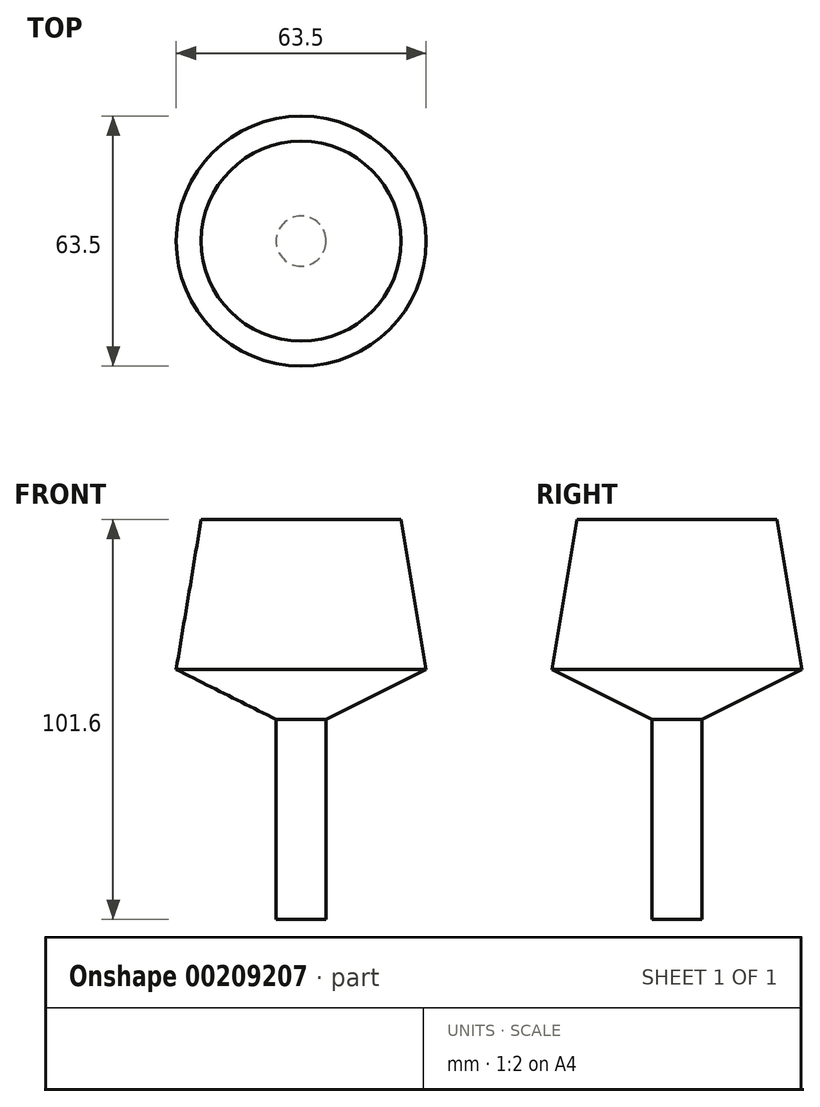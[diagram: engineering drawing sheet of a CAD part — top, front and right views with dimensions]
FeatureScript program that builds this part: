
annotation { "Feature Type Name" : "Feature", "Feature Type Description" : "" }
export const myFeature = defineFeature(function(context is Context, id is Id, definition is map)
    precondition{}
    {
        {
            var Q0;
            Q0=qCreatedBy(makeId("Front.planeOp"),FACE);
            var sketch = newSketch(context, id + "F0", { "sketchPlane" : qUnion([Q0])});
            skLineSegment(sketch, "E0", {"start": v(0, 0) * mm, "end": v(0, 101.6) * mm});
            skLineSegment(sketch, "E1", {"start": v(0, 101.6) * mm, "end": v(25.4, 101.6) * mm});
            skLineSegment(sketch, "E2", {"start": v(25.4, 101.6) * mm, "end": v(31.75, 63.5) * mm});
            skLineSegment(sketch, "E3", {"start": v(31.75, 63.5) * mm, "end": v(6.35, 50.8) * mm});
            skLineSegment(sketch, "E4", {"start": v(6.35, 50.8) * mm, "end": v(6.35, 0) * mm});
            skLineSegment(sketch, "E5", {"start": v(6.35, 0) * mm, "end": v(0, 0) * mm});
            skSolve(sketch);
        }
        {
            var Q0;
            Q0 = qSketchRegion(id + "F0", true);
            var Q1;
            Q1=sQuery(id+"F0.wireOp",EDGE,"E0");
            revolve(context, id + "F1", {"entities" : qUnion([Q0]), "axis" : qUnion([Q1]), "revolveType" : RevolveType.FULL});
        }
    });
